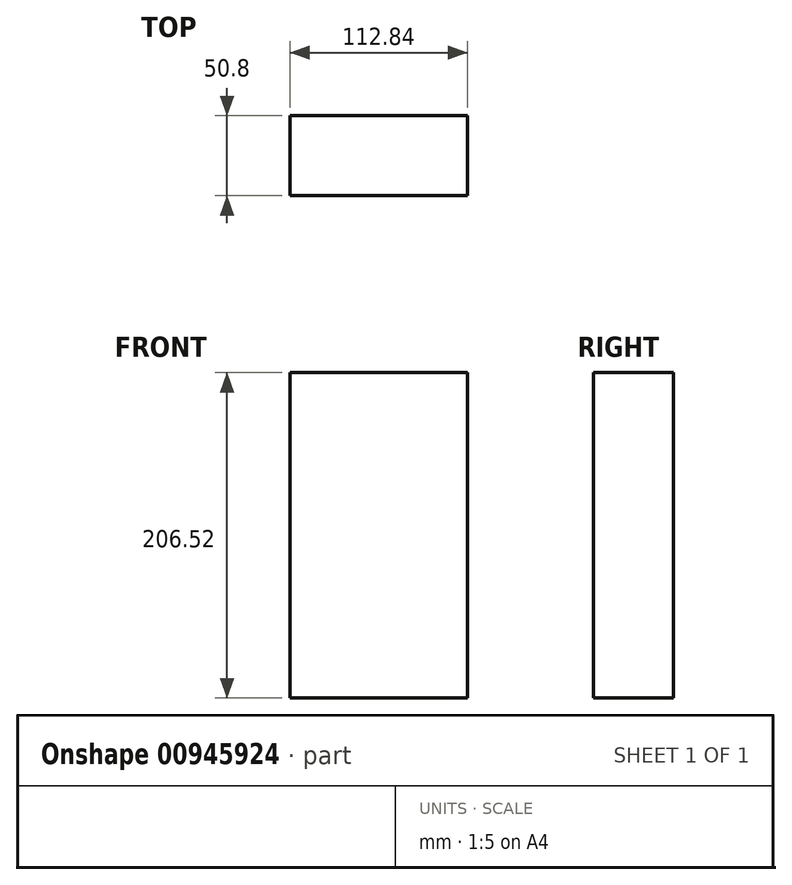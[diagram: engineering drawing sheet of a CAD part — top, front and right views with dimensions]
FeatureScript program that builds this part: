
annotation { "Feature Type Name" : "Feature", "Feature Type Description" : "" }
export const myFeature = defineFeature(function(context is Context, id is Id, definition is map)
    precondition{}
    {
        {
            var Q0;
            Q0=qCreatedBy(makeId("Front.planeOp"),FACE);
            var sketch = newSketch(context, id + "F0", { "sketchPlane" : qUnion([Q0])});
            skLineSegment(sketch, "E0.bottom", {"start": v(-56.42, 103.26) * mm, "end": v(56.42, 103.26) * mm});
            skLineSegment(sketch, "E0.top", {"start": v(-56.42, -103.26) * mm, "end": v(56.42, -103.26) * mm});
            skLineSegment(sketch, "E0.left", {"start": v(-56.42, 103.26) * mm, "end": v(-56.42, -103.26) * mm});
            skLineSegment(sketch, "E0.right", {"start": v(56.42, 103.26) * mm, "end": v(56.42, -103.26) * mm});
            skPoint(sketch, "E0.middle", {"position": v(0, 0) * mm});
            skSolve(sketch);
        }
        {
            var Q0;
            Q0=makeQuery(id+"F0.imprint","IMPRINT",FACE,{"disambiguationData":[TD([[makeQuery(id+"F0.imprint","IMPRINT",EDGE,{"derivedFrom":sQuery(id+"F0.wireOp",EDGE,"E0.bottom")}),-1.0]])]});
            extrude(context, id + "F1", {"entities" : qUnion([Q0]), "depth" : 50.8 * mm, "offsetDistance" : 25.4 * mm});
        }
    });
